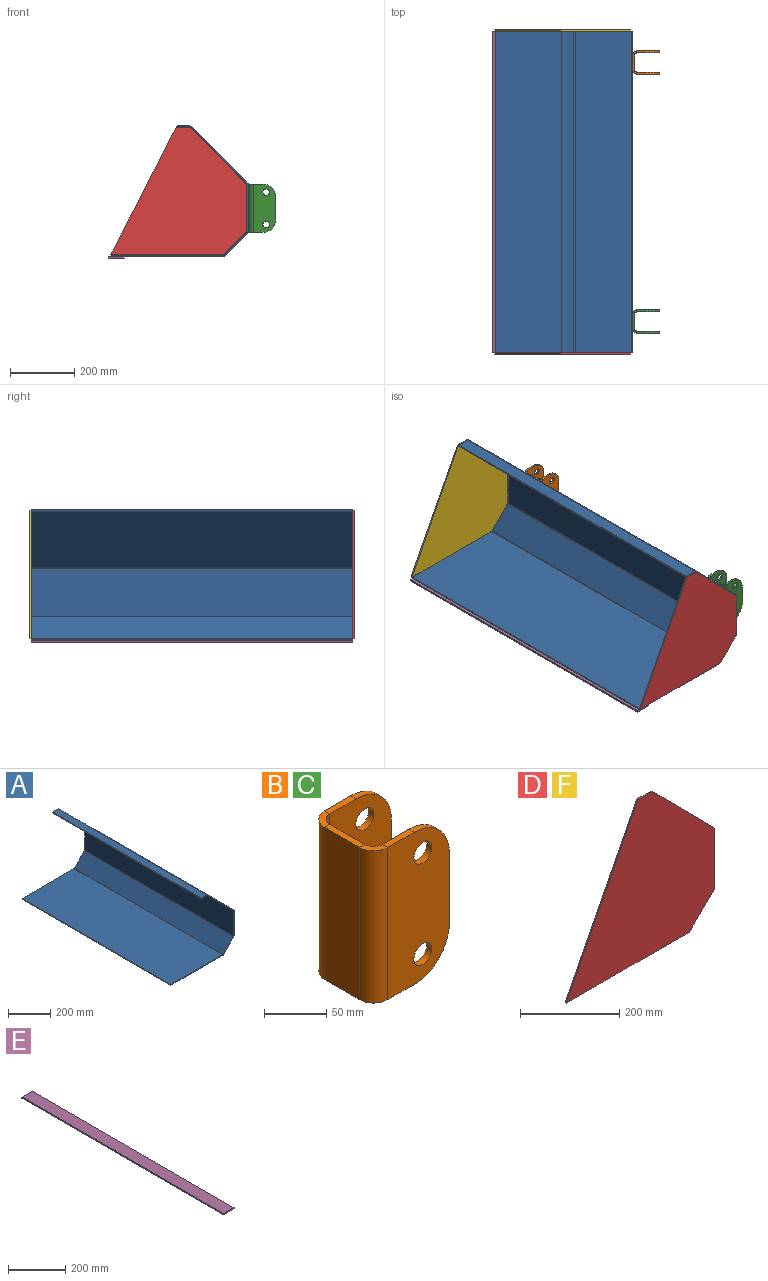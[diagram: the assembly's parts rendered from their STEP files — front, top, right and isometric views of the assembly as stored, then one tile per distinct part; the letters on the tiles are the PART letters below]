
ASSEMBLY  parts=6 mates=5
PART A: 38 faces, bbox 424.7x1000x405.5 mm
  f0: plane 349.05x4mm, normal (0,1,0), area 1396.2mm2, adj f2,f3,f4,f35
  f1: plane 349.05x4mm, normal (0,-1,0), area 1396.2mm2, adj f2,f3,f4,f34
  f2: plane 1000x4mm, normal (-1,0,0), area 4000mm2, adj f0,f1,f3,f4
  f3: plane 1000x349.05mm, normal (0,0,-1), area 349047.3mm2, adj f0,f1,f2,f36
  f4: plane 1000x349.05mm, normal (0,0,1), area 349047.3mm2, adj f0,f1,f2,f37
  f5: plane 72.19x72.19mm, normal (0,1,0), area 392.4mm2, adj f7,f8,f31,f35
  f6: plane 72.19x72.19mm, normal (0,-1,0), area 392.4mm2, adj f7,f8,f30,f34
  f7: plane 1000x69.36mm, normal (0.71,0,-0.71), area 98094.6mm2, adj f5,f6,f32,f36
  f8: plane 1000x69.36mm, normal (-0.71,0,0.71), area 98094.6mm2, adj f5,f6,f33,f37
  f9: plane 148.09x4mm, normal (0,1,0), area 592.4mm2, adj f11,f12,f27,f31
  f10: plane 148.09x4mm, normal (0,-1,0), area 592.4mm2, adj f11,f12,f26,f30
  f11: plane 1000x148.09mm, normal (1,0,0), area 148094.6mm2, adj f9,f10,f28,f32
  f12: plane 1000x148.09mm, normal (-1,0,0), area 148094.6mm2, adj f9,f10,f29,f33
  f13: plane 178.26x178.26mm, normal (0,1,0), area 992.4mm2, adj f15,f16,f23,f27
  f14: plane 178.26x178.26mm, normal (0,-1,0), area 992.4mm2, adj f15,f16,f22,f26
  f15: plane 1000x175.43mm, normal (0.71,0,0.71), area 248094.6mm2, adj f13,f14,f24,f28
  f16: plane 1000x175.43mm, normal (-0.71,0,-0.71), area 248094.6mm2, adj f13,f14,f25,f29
  f17: plane 39.05x4mm, normal (0,1,0), area 156.2mm2, adj f18,f20,f21,f23
  f18: plane 1000x4mm, normal (-1,0,0), area 4000mm2, adj f17,f19,f20,f21
  f19: plane 39.05x4mm, normal (0,-1,0), area 156.2mm2, adj f18,f20,f21,f22
  f20: plane 1000x39.05mm, normal (0,0,1), area 39047.3mm2, adj f17,f18,f19,f24
  f21: plane 1000x39.05mm, normal (0,0,-1), area 39047.3mm2, adj f17,f18,f19,f25
  f22: plane 4.67x4.45mm, normal (0,-1,0), area 13.5mm2, adj f14,f19,f24,f25
  f23: plane 4.67x4.45mm, normal (0,1,0), area 13.5mm2, adj f13,f17,f24,f25
  f24: cylinder r=6.3mm len=1000mm, axis (0,-1,0), area 4948mm2, adj f15,f20,f22,f23
  f25: cylinder r=2.3mm len=1000mm, axis (0,-1,0), area 1806.4mm2, adj f16,f21,f22,f23
  f26: plane 4.67x4.45mm, normal (0,-1,0), area 13.5mm2, adj f10,f14,f28,f29
  f27: plane 4.67x4.45mm, normal (0,1,0), area 13.5mm2, adj f9,f13,f28,f29
  f28: cylinder r=6.3mm len=1000mm, axis (0,-1,0), area 4948mm2, adj f11,f15,f26,f27
  f29: cylinder r=2.3mm len=1000mm, axis (0,-1,0), area 1806.4mm2, adj f12,f16,f26,f27
  f30: plane 4.67x4.45mm, normal (0,-1,0), area 13.5mm2, adj f6,f10,f32,f33
  f31: plane 4.67x4.45mm, normal (0,1,0), area 13.5mm2, adj f5,f9,f32,f33
  f32: cylinder r=6.3mm len=1000mm, axis (0,-1,0), area 4948mm2, adj f7,f11,f30,f31
  f33: cylinder r=2.3mm len=1000mm, axis (0,-1,0), area 1806.4mm2, adj f8,f12,f30,f31
  f34: plane 4.67x4.45mm, normal (0,-1,0), area 13.5mm2, adj f1,f6,f36,f37
  f35: plane 4.67x4.45mm, normal (0,1,0), area 13.5mm2, adj f0,f5,f36,f37
  f36: cylinder r=6.3mm len=1000mm, axis (0,-1,0), area 4948mm2, adj f3,f7,f34,f35
  f37: cylinder r=2.3mm len=1000mm, axis (0,-1,0), area 1806.4mm2, adj f4,f8,f34,f35
PART B: 30 faces, bbox 86x72x150 mm
  f0: plane 30x6mm, normal (0,0,-1), area 180mm2, adj f5,f6,f8,f27
  f1: plane 30x6mm, normal (0,0,1), area 180mm2, adj f5,f6,f7,f26
  f2: cylinder r=10.25mm len=20.5mm, axis (0,1,0), area 386.4mm2, adj f5,f6
  f3: cylinder r=10.25mm len=20.5mm, axis (0,1,0), area 386.4mm2, adj f5,f6
  f4: plane 70x6mm, normal (1,0,0), area 420mm2, adj f5,f6,f7,f8
  f5: plane 150x70mm, normal (0,1,0), area 9153.1mm2, adj f0,f1,f2,f3,f4,f7,f8,f28
  f6: plane 150x70mm, normal (0,-1,0), area 9153.1mm2, adj f0,f1,f2,f3,f4,f7,f8,f29
  f7: cylinder r=40mm len=40mm, axis (0,1,0), area 377mm2, adj f1,f4,f5,f6
  f8: cylinder r=40mm len=40mm, axis (0,-1,0), area 377mm2, adj f0,f4,f5,f6
  f9: plane 40x6mm, normal (0,0,-1), area 240mm2, adj f11,f12,f23,f27
  f10: plane 40x6mm, normal (0,0,1), area 240mm2, adj f11,f12,f22,f26
  f11: plane 150x40mm, normal (-1,0,0), area 6000mm2, adj f9,f10,f24,f28
  f12: plane 150x40mm, normal (1,0,0), area 6000mm2, adj f9,f10,f25,f29
  f13: plane 30x6mm, normal (0,0,-1), area 180mm2, adj f18,f19,f20,f23
  f14: plane 70x6mm, normal (1,0,0), area 420mm2, adj f18,f19,f20,f21
  f15: plane 30x6mm, normal (0,0,1), area 180mm2, adj f18,f19,f21,f22
  f16: cylinder r=10.25mm len=20.5mm, axis (0,-1,0), area 386.4mm2, adj f18,f19
  f17: cylinder r=10.25mm len=20.5mm, axis (0,-1,0), area 386.4mm2, adj f18,f19
  f18: plane 150x70mm, normal (0,-1,0), area 9153.1mm2, adj f13,f14,f15,f16,f17,f20,f21,f24
  f19: plane 150x70mm, normal (0,1,0), area 9153.1mm2, adj f13,f14,f15,f16,f17,f20,f21,f25
  f20: cylinder r=40mm len=40mm, axis (0,-1,0), area 377mm2, adj f13,f14,f18,f19
  f21: cylinder r=40mm len=40mm, axis (0,1,0), area 377mm2, adj f14,f15,f18,f19
  f22: plane 16x16mm, normal (0,0,1), area 122.5mm2, adj f10,f15,f24,f25
  f23: plane 16x16mm, normal (0,0,-1), area 122.5mm2, adj f9,f13,f24,f25
  f24: cylinder r=16mm len=150mm, axis (0,0,1), area 3769.9mm2, adj f11,f18,f22,f23
  f25: cylinder r=10mm len=150mm, axis (0,0,1), area 2356.2mm2, adj f12,f19,f22,f23
  f26: plane 16x16mm, normal (0,0,1), area 122.5mm2, adj f1,f10,f28,f29
  f27: plane 16x16mm, normal (0,0,-1), area 122.5mm2, adj f0,f9,f28,f29
  f28: cylinder r=16mm len=150mm, axis (0,0,1), area 3769.9mm2, adj f5,f11,f26,f27
  f29: cylinder r=10mm len=150mm, axis (0,0,1), area 2356.2mm2, adj f6,f12,f26,f27
PART C: same geometry as B
PART D: 8 faces, bbox 422.7x4x399.5 mm
  f0: plane 350x4mm, normal (0,0,-1), area 1400mm2, adj f1,f5,f6,f7
  f1: plane 72.71x71.66mm, normal (0.7,0,-0.71), area 408.4mm2, adj f0,f2,f6,f7
  f2: plane 148.09x4mm, normal (1,0,0), area 592.4mm2, adj f1,f3,f6,f7
  f3: plane 178.47x176.69mm, normal (0.71,0,0.7), area 1004.6mm2, adj f2,f4,f6,f7
  f4: plane 42.09x4mm, normal (0.03,0,1), area 168.4mm2, adj f3,f5,f6,f7
  f5: plane 399.49x203.93mm, normal (-0.89,0,0.45), area 1794.1mm2, adj f0,f4,f6,f7
  f6: plane 422.71x399.49mm, normal (0,-1,0), area 109511.9mm2, adj f0,f1,f2,f3,f4,f5
  f7: plane 422.71x399.49mm, normal (0,1,0), area 109511.9mm2, adj f0,f1,f2,f3,f4,f5
PART E: 6 faces, bbox 50x1000x5 mm
  f0: plane 1000x5mm, normal (1,0,0), area 5000mm2, adj f1,f3,f4,f5
  f1: plane 50x5mm, normal (0,-1,0), area 250mm2, adj f0,f2,f4,f5
  f2: plane 1000x5mm, normal (-1,0,0), area 5000mm2, adj f1,f3,f4,f5
  f3: plane 50x5mm, normal (0,1,0), area 250mm2, adj f0,f2,f4,f5
  f4: plane 1000x50mm, normal (0,0,-1), area 50000mm2, adj f0,f1,f2,f3
  f5: plane 1000x50mm, normal (0,0,1), area 50000mm2, adj f0,f1,f2,f3
PART F: same geometry as D
PLACE A t=(-74.71,0,-145.71)mm
PLACE B t=(-74.71,402.5,-145)mm
PLACE C t=(-74.71,-402.5,-145)mm
PLACE D t=(-76.23,0,-145.08)mm
PLACE E t=(-84.71,0,-145.71)mm
PLACE F t=(-76.23,1004,-145.08)mm
MATE fastened B.f11 <-> A.f11  axis (-1,0,0) through (0,402.5,0)mm
MATE fastened A.f11 <-> C.f11  axis (1,0,0) through (0,0,0)mm
MATE fastened A.f19 <-> D.f7  axis (0,-1,0) through (-201.25,-500,253.78)mm
MATE fastened E.f5 <-> A.f3  axis (0,0,1) through (-434.71,0,-149.71)mm
MATE fastened A.f17 <-> F.f6  axis (0,1,0) through (-201.25,500,253.78)mm
